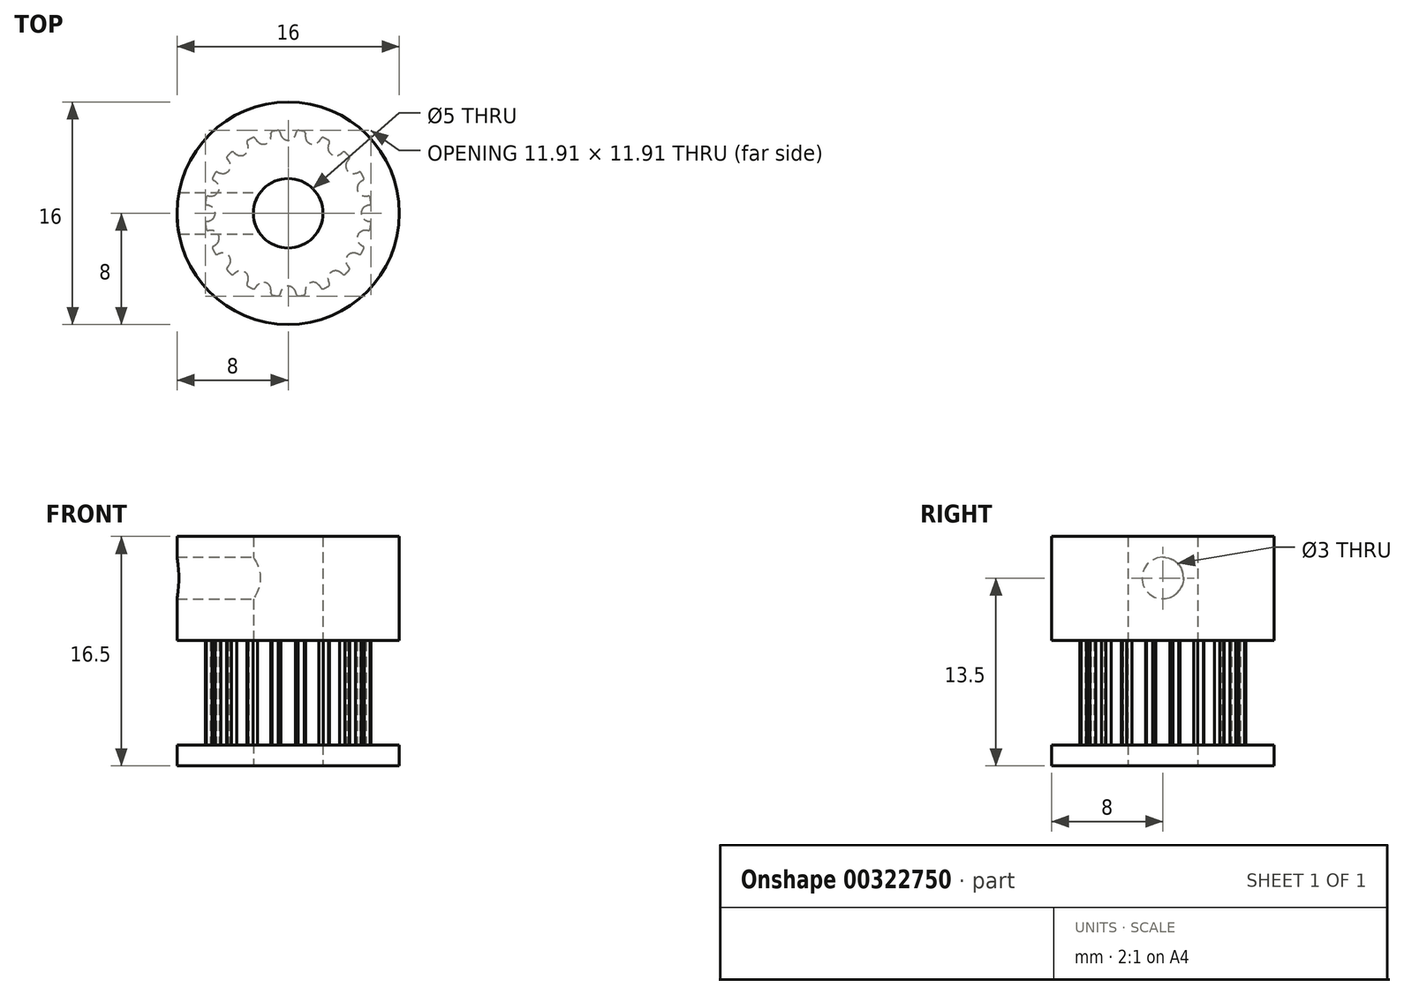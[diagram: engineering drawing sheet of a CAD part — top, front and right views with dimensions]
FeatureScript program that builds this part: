
annotation { "Feature Type Name" : "Feature", "Feature Type Description" : "" }
export const myFeature = defineFeature(function(context is Context, id is Id, definition is map)
    precondition{}
    {
        {
            var Q0;
            Q0=qCreatedBy(makeId("Top.planeOp"),FACE);
            var sketch = newSketch(context, id + "F0", { "sketchPlane" : qUnion([Q0])});
            skLineSegment(sketch, "E0", {"start": v(-19.17, 17.78) * mm, "end": v(-18.17, 17.78) * mm});
            skLineSegment(sketch, "E1", {"start": v(-18.17, 17.78) * mm, "end": v(-18.17, 18.4) * mm});
            skArc(sketch, "E2", {"start": v(-18.67, 18.85) * mm, "mid": v(-18.88, 19.07) * mm, "end": v(-19.17, 19.16) * mm});
            skArc(sketch, "E3", {"start": v(-18.58, 18.54) * mm, "mid": v(-18.61, 18.7) * mm, "end": v(-18.67, 18.85) * mm});
            skArc(sketch, "E4", {"start": v(-18.58, 18.54) * mm, "mid": v(-18.53, 18.44) * mm, "end": v(-18.43, 18.4) * mm});
            skLineSegment(sketch, "E5", {"start": v(-18.43, 18.4) * mm, "end": v(-18.17, 18.4) * mm});
            skArc(sketch, "E6.0.MirrorCS", {"start": v(-19.67, 18.85) * mm, "mid": v(-19.47, 19.07) * mm, "end": v(-19.17, 19.16) * mm});
            skArc(sketch, "E7.0.MirrorCS", {"start": v(-19.76, 18.54) * mm, "mid": v(-19.73, 18.7) * mm, "end": v(-19.67, 18.85) * mm});
            skArc(sketch, "E8.0.MirrorCS", {"start": v(-19.76, 18.54) * mm, "mid": v(-19.81, 18.44) * mm, "end": v(-19.91, 18.4) * mm});
            skLineSegment(sketch, "E9.0.MirrorCS", {"start": v(-19.91, 18.4) * mm, "end": v(-20.17, 18.4) * mm});
            skLineSegment(sketch, "E10.0.MirrorCS", {"start": v(-20.17, 17.78) * mm, "end": v(-20.17, 18.4) * mm});
            skLineSegment(sketch, "E11.0.MirrorCS", {"start": v(-19.17, 17.78) * mm, "end": v(-20.17, 17.78) * mm});
            skLineSegment(sketch, "E12.direction1", {"start": v(-20.17, 17.78) * mm, "end": v(-18.17, 17.78) * mm, "construction": true});
            skLineSegment(sketch, "E13", {"start": v(-20.17, 18.15) * mm, "end": v(-18.17, 18.15) * mm, "construction": true});
            skPoint(sketch, "E14", {"position": v(0, -5.25) * mm});
            skArc(sketch, "E15", {"start": v(0.51, -5.6) * mm, "mid": v(0, -5.25) * mm, "end": v(-0.51, -5.6) * mm});
            skArc(sketch, "E16", {"start": v(-0.51, -5.6) * mm, "mid": v(-0.56, -5.71) * mm, "end": v(-0.59, -5.83) * mm});
            skArc(sketch, "E17", {"start": v(0.59, -5.83) * mm, "mid": v(0.56, -5.71) * mm, "end": v(0.51, -5.6) * mm});
            skArc(sketch, "E18", {"start": v(0.72, -5.96) * mm, "mid": v(0.94, -5.93) * mm, "end": v(1.16, -5.89) * mm});
            skArc(sketch, "E19", {"start": v(0.59, -5.83) * mm, "mid": v(0.66, -5.94) * mm, "end": v(0.8, -5.95) * mm});
            skArc(sketch, "E20", {"start": v(-0.59, -5.83) * mm, "mid": v(-0.66, -5.94) * mm, "end": v(-0.8, -5.95) * mm});
            skArc(sketch, "E21.1.0", {"start": v(2.22, -5.16) * mm, "mid": v(1.62, -5) * mm, "end": v(1.24, -5.48) * mm});
            skPoint(sketch, "E21.1.1", {"position": v(1.62, -5) * mm});
            skArc(sketch, "E21.1.2", {"start": v(1.24, -5.48) * mm, "mid": v(1.23, -5.6) * mm, "end": v(1.24, -5.73) * mm});
            skArc(sketch, "E21.1.3", {"start": v(2.36, -5.37) * mm, "mid": v(2.47, -5.44) * mm, "end": v(2.6, -5.41) * mm});
            skArc(sketch, "E21.1.4", {"start": v(1.24, -5.73) * mm, "mid": v(1.2, -5.85) * mm, "end": v(1.08, -5.9) * mm});
            skArc(sketch, "E21.1.5", {"start": v(2.36, -5.37) * mm, "mid": v(2.3, -5.26) * mm, "end": v(2.22, -5.16) * mm});
            skArc(sketch, "E22.3.2.0", {"start": v(3.7, -4.22) * mm, "mid": v(3.09, -4.25) * mm, "end": v(2.87, -4.83) * mm});
            skPoint(sketch, "E22.4.2.0", {"position": v(3.09, -4.25) * mm});
            skArc(sketch, "E22.5.2.0", {"start": v(2.87, -4.83) * mm, "mid": v(2.9, -4.95) * mm, "end": v(2.95, -5.07) * mm});
            skArc(sketch, "E22.9.2.0", {"start": v(3.9, -4.37) * mm, "mid": v(4.03, -4.41) * mm, "end": v(4.14, -4.35) * mm});
            skArc(sketch, "E22.13.2.0", {"start": v(2.95, -5.07) * mm, "mid": v(2.95, -5.2) * mm, "end": v(2.85, -5.28) * mm});
            skArc(sketch, "E22.17.2.0", {"start": v(3.9, -4.37) * mm, "mid": v(3.81, -4.3) * mm, "end": v(3.7, -4.22) * mm});
            skArc(sketch, "E22.3.3.0", {"start": v(4.83, -2.87) * mm, "mid": v(4.25, -3.09) * mm, "end": v(4.22, -3.7) * mm});
            skPoint(sketch, "E22.4.3.0", {"position": v(4.25, -3.09) * mm});
            skArc(sketch, "E22.5.3.0", {"start": v(4.22, -3.7) * mm, "mid": v(4.3, -3.81) * mm, "end": v(4.37, -3.9) * mm});
            skArc(sketch, "E22.9.3.0", {"start": v(5.07, -2.95) * mm, "mid": v(5.2, -2.95) * mm, "end": v(5.28, -2.85) * mm});
            skArc(sketch, "E22.13.3.0", {"start": v(4.37, -3.9) * mm, "mid": v(4.41, -4.03) * mm, "end": v(4.35, -4.14) * mm});
            skArc(sketch, "E22.17.3.0", {"start": v(5.07, -2.95) * mm, "mid": v(4.95, -2.9) * mm, "end": v(4.83, -2.87) * mm});
            skArc(sketch, "E22.3.4.0", {"start": v(5.48, -1.24) * mm, "mid": v(5, -1.62) * mm, "end": v(5.16, -2.22) * mm});
            skPoint(sketch, "E22.4.4.0", {"position": v(5, -1.62) * mm});
            skArc(sketch, "E22.5.4.0", {"start": v(5.16, -2.22) * mm, "mid": v(5.26, -2.3) * mm, "end": v(5.37, -2.36) * mm});
            skArc(sketch, "E22.9.4.0", {"start": v(5.73, -1.24) * mm, "mid": v(5.85, -1.2) * mm, "end": v(5.9, -1.08) * mm});
            skArc(sketch, "E22.13.4.0", {"start": v(5.37, -2.36) * mm, "mid": v(5.44, -2.47) * mm, "end": v(5.41, -2.6) * mm});
            skArc(sketch, "E22.17.4.0", {"start": v(5.73, -1.24) * mm, "mid": v(5.6, -1.23) * mm, "end": v(5.48, -1.24) * mm});
            skArc(sketch, "E22.3.5.0", {"start": v(5.6, 0.51) * mm, "mid": v(5.25, 0) * mm, "end": v(5.6, -0.51) * mm});
            skPoint(sketch, "E22.4.5.0", {"position": v(5.25, 0) * mm});
            skArc(sketch, "E22.5.5.0", {"start": v(5.6, -0.51) * mm, "mid": v(5.71, -0.56) * mm, "end": v(5.83, -0.59) * mm});
            skArc(sketch, "E22.9.5.0", {"start": v(5.83, 0.59) * mm, "mid": v(5.94, 0.66) * mm, "end": v(5.95, 0.8) * mm});
            skArc(sketch, "E22.13.5.0", {"start": v(5.83, -0.59) * mm, "mid": v(5.94, -0.66) * mm, "end": v(5.95, -0.8) * mm});
            skArc(sketch, "E22.17.5.0", {"start": v(5.83, 0.59) * mm, "mid": v(5.71, 0.56) * mm, "end": v(5.6, 0.51) * mm});
            skArc(sketch, "E22.3.6.0", {"start": v(5.16, 2.22) * mm, "mid": v(5, 1.62) * mm, "end": v(5.48, 1.24) * mm});
            skPoint(sketch, "E22.4.6.0", {"position": v(5, 1.62) * mm});
            skArc(sketch, "E22.5.6.0", {"start": v(5.48, 1.24) * mm, "mid": v(5.6, 1.23) * mm, "end": v(5.73, 1.24) * mm});
            skArc(sketch, "E22.9.6.0", {"start": v(5.37, 2.36) * mm, "mid": v(5.44, 2.47) * mm, "end": v(5.41, 2.6) * mm});
            skArc(sketch, "E22.13.6.0", {"start": v(5.73, 1.24) * mm, "mid": v(5.85, 1.2) * mm, "end": v(5.9, 1.08) * mm});
            skArc(sketch, "E22.17.6.0", {"start": v(5.37, 2.36) * mm, "mid": v(5.26, 2.3) * mm, "end": v(5.16, 2.22) * mm});
            skArc(sketch, "E22.3.7.0", {"start": v(4.22, 3.7) * mm, "mid": v(4.25, 3.09) * mm, "end": v(4.83, 2.87) * mm});
            skPoint(sketch, "E22.4.7.0", {"position": v(4.25, 3.09) * mm});
            skArc(sketch, "E22.5.7.0", {"start": v(4.83, 2.87) * mm, "mid": v(4.95, 2.9) * mm, "end": v(5.07, 2.95) * mm});
            skArc(sketch, "E22.9.7.0", {"start": v(4.37, 3.9) * mm, "mid": v(4.41, 4.03) * mm, "end": v(4.35, 4.14) * mm});
            skArc(sketch, "E22.13.7.0", {"start": v(5.07, 2.95) * mm, "mid": v(5.2, 2.95) * mm, "end": v(5.28, 2.85) * mm});
            skArc(sketch, "E22.17.7.0", {"start": v(4.37, 3.9) * mm, "mid": v(4.3, 3.81) * mm, "end": v(4.22, 3.7) * mm});
            skArc(sketch, "E22.3.8.0", {"start": v(2.87, 4.83) * mm, "mid": v(3.09, 4.25) * mm, "end": v(3.7, 4.22) * mm});
            skPoint(sketch, "E22.4.8.0", {"position": v(3.09, 4.25) * mm});
            skArc(sketch, "E22.5.8.0", {"start": v(3.7, 4.22) * mm, "mid": v(3.81, 4.3) * mm, "end": v(3.9, 4.37) * mm});
            skArc(sketch, "E22.9.8.0", {"start": v(2.95, 5.07) * mm, "mid": v(2.95, 5.2) * mm, "end": v(2.85, 5.28) * mm});
            skArc(sketch, "E22.13.8.0", {"start": v(3.9, 4.37) * mm, "mid": v(4.03, 4.41) * mm, "end": v(4.14, 4.35) * mm});
            skArc(sketch, "E22.17.8.0", {"start": v(2.95, 5.07) * mm, "mid": v(2.9, 4.95) * mm, "end": v(2.87, 4.83) * mm});
            skArc(sketch, "E22.3.9.0", {"start": v(1.24, 5.48) * mm, "mid": v(1.62, 5) * mm, "end": v(2.22, 5.16) * mm});
            skPoint(sketch, "E22.4.9.0", {"position": v(1.62, 5) * mm});
            skArc(sketch, "E22.5.9.0", {"start": v(2.22, 5.16) * mm, "mid": v(2.3, 5.26) * mm, "end": v(2.36, 5.37) * mm});
            skArc(sketch, "E22.9.9.0", {"start": v(1.24, 5.73) * mm, "mid": v(1.2, 5.85) * mm, "end": v(1.08, 5.9) * mm});
            skArc(sketch, "E22.13.9.0", {"start": v(2.36, 5.37) * mm, "mid": v(2.47, 5.44) * mm, "end": v(2.6, 5.41) * mm});
            skArc(sketch, "E22.17.9.0", {"start": v(1.24, 5.73) * mm, "mid": v(1.23, 5.6) * mm, "end": v(1.24, 5.48) * mm});
            skArc(sketch, "E22.3.10.0", {"start": v(-0.51, 5.6) * mm, "mid": v(0, 5.25) * mm, "end": v(0.51, 5.6) * mm});
            skPoint(sketch, "E22.4.10.0", {"position": v(0, 5.25) * mm});
            skArc(sketch, "E22.5.10.0", {"start": v(0.51, 5.6) * mm, "mid": v(0.56, 5.71) * mm, "end": v(0.59, 5.83) * mm});
            skArc(sketch, "E22.9.10.0", {"start": v(-0.59, 5.83) * mm, "mid": v(-0.66, 5.94) * mm, "end": v(-0.8, 5.95) * mm});
            skArc(sketch, "E22.13.10.0", {"start": v(0.59, 5.83) * mm, "mid": v(0.66, 5.94) * mm, "end": v(0.8, 5.95) * mm});
            skArc(sketch, "E22.17.10.0", {"start": v(-0.59, 5.83) * mm, "mid": v(-0.56, 5.71) * mm, "end": v(-0.51, 5.6) * mm});
            skArc(sketch, "E22.3.11.0", {"start": v(-2.22, 5.16) * mm, "mid": v(-1.62, 5) * mm, "end": v(-1.24, 5.48) * mm});
            skPoint(sketch, "E22.4.11.0", {"position": v(-1.62, 5) * mm});
            skArc(sketch, "E22.5.11.0", {"start": v(-1.24, 5.48) * mm, "mid": v(-1.23, 5.6) * mm, "end": v(-1.24, 5.73) * mm});
            skArc(sketch, "E22.9.11.0", {"start": v(-2.36, 5.37) * mm, "mid": v(-2.47, 5.44) * mm, "end": v(-2.6, 5.41) * mm});
            skArc(sketch, "E22.13.11.0", {"start": v(-1.24, 5.73) * mm, "mid": v(-1.2, 5.85) * mm, "end": v(-1.08, 5.9) * mm});
            skArc(sketch, "E22.17.11.0", {"start": v(-2.36, 5.37) * mm, "mid": v(-2.3, 5.26) * mm, "end": v(-2.22, 5.16) * mm});
            skArc(sketch, "E22.3.12.0", {"start": v(-3.7, 4.22) * mm, "mid": v(-3.09, 4.25) * mm, "end": v(-2.87, 4.83) * mm});
            skPoint(sketch, "E22.4.12.0", {"position": v(-3.09, 4.25) * mm});
            skArc(sketch, "E22.5.12.0", {"start": v(-2.87, 4.83) * mm, "mid": v(-2.9, 4.95) * mm, "end": v(-2.95, 5.07) * mm});
            skArc(sketch, "E22.9.12.0", {"start": v(-3.9, 4.37) * mm, "mid": v(-4.03, 4.41) * mm, "end": v(-4.14, 4.35) * mm});
            skArc(sketch, "E22.13.12.0", {"start": v(-2.95, 5.07) * mm, "mid": v(-2.95, 5.2) * mm, "end": v(-2.85, 5.28) * mm});
            skArc(sketch, "E22.17.12.0", {"start": v(-3.9, 4.37) * mm, "mid": v(-3.81, 4.3) * mm, "end": v(-3.7, 4.22) * mm});
            skArc(sketch, "E22.3.13.0", {"start": v(-4.83, 2.87) * mm, "mid": v(-4.25, 3.09) * mm, "end": v(-4.22, 3.7) * mm});
            skPoint(sketch, "E22.4.13.0", {"position": v(-4.25, 3.09) * mm});
            skArc(sketch, "E22.5.13.0", {"start": v(-4.22, 3.7) * mm, "mid": v(-4.3, 3.81) * mm, "end": v(-4.37, 3.9) * mm});
            skArc(sketch, "E22.9.13.0", {"start": v(-5.07, 2.95) * mm, "mid": v(-5.2, 2.95) * mm, "end": v(-5.28, 2.85) * mm});
            skArc(sketch, "E22.13.13.0", {"start": v(-4.37, 3.9) * mm, "mid": v(-4.41, 4.03) * mm, "end": v(-4.35, 4.14) * mm});
            skArc(sketch, "E22.17.13.0", {"start": v(-5.07, 2.95) * mm, "mid": v(-4.95, 2.9) * mm, "end": v(-4.83, 2.87) * mm});
            skArc(sketch, "E22.3.14.0", {"start": v(-5.48, 1.24) * mm, "mid": v(-5, 1.62) * mm, "end": v(-5.16, 2.22) * mm});
            skPoint(sketch, "E22.4.14.0", {"position": v(-5, 1.62) * mm});
            skArc(sketch, "E22.5.14.0", {"start": v(-5.16, 2.22) * mm, "mid": v(-5.26, 2.3) * mm, "end": v(-5.37, 2.36) * mm});
            skArc(sketch, "E22.9.14.0", {"start": v(-5.73, 1.24) * mm, "mid": v(-5.85, 1.2) * mm, "end": v(-5.9, 1.08) * mm});
            skArc(sketch, "E22.13.14.0", {"start": v(-5.37, 2.36) * mm, "mid": v(-5.44, 2.47) * mm, "end": v(-5.41, 2.6) * mm});
            skArc(sketch, "E22.17.14.0", {"start": v(-5.73, 1.24) * mm, "mid": v(-5.6, 1.23) * mm, "end": v(-5.48, 1.24) * mm});
            skArc(sketch, "E22.3.15.0", {"start": v(-5.6, -0.51) * mm, "mid": v(-5.25, 0) * mm, "end": v(-5.6, 0.51) * mm});
            skPoint(sketch, "E22.4.15.0", {"position": v(-5.25, 0) * mm});
            skArc(sketch, "E22.5.15.0", {"start": v(-5.6, 0.51) * mm, "mid": v(-5.71, 0.56) * mm, "end": v(-5.83, 0.59) * mm});
            skArc(sketch, "E22.9.15.0", {"start": v(-5.83, -0.59) * mm, "mid": v(-5.94, -0.66) * mm, "end": v(-5.95, -0.8) * mm});
            skArc(sketch, "E22.13.15.0", {"start": v(-5.83, 0.59) * mm, "mid": v(-5.94, 0.66) * mm, "end": v(-5.95, 0.8) * mm});
            skArc(sketch, "E22.17.15.0", {"start": v(-5.83, -0.59) * mm, "mid": v(-5.71, -0.56) * mm, "end": v(-5.6, -0.51) * mm});
            skArc(sketch, "E22.3.16.0", {"start": v(-5.16, -2.22) * mm, "mid": v(-5, -1.62) * mm, "end": v(-5.48, -1.24) * mm});
            skPoint(sketch, "E22.4.16.0", {"position": v(-5, -1.62) * mm});
            skArc(sketch, "E22.5.16.0", {"start": v(-5.48, -1.24) * mm, "mid": v(-5.6, -1.23) * mm, "end": v(-5.73, -1.24) * mm});
            skArc(sketch, "E22.9.16.0", {"start": v(-5.37, -2.36) * mm, "mid": v(-5.44, -2.47) * mm, "end": v(-5.41, -2.6) * mm});
            skArc(sketch, "E22.13.16.0", {"start": v(-5.73, -1.24) * mm, "mid": v(-5.85, -1.2) * mm, "end": v(-5.9, -1.08) * mm});
            skArc(sketch, "E22.17.16.0", {"start": v(-5.37, -2.36) * mm, "mid": v(-5.26, -2.3) * mm, "end": v(-5.16, -2.22) * mm});
            skArc(sketch, "E22.3.17.0", {"start": v(-4.22, -3.7) * mm, "mid": v(-4.25, -3.09) * mm, "end": v(-4.83, -2.87) * mm});
            skPoint(sketch, "E22.4.17.0", {"position": v(-4.25, -3.09) * mm});
            skArc(sketch, "E22.5.17.0", {"start": v(-4.83, -2.87) * mm, "mid": v(-4.95, -2.9) * mm, "end": v(-5.07, -2.95) * mm});
            skArc(sketch, "E22.9.17.0", {"start": v(-4.37, -3.9) * mm, "mid": v(-4.41, -4.03) * mm, "end": v(-4.35, -4.14) * mm});
            skArc(sketch, "E22.13.17.0", {"start": v(-5.07, -2.95) * mm, "mid": v(-5.2, -2.95) * mm, "end": v(-5.28, -2.85) * mm});
            skArc(sketch, "E22.17.17.0", {"start": v(-4.37, -3.9) * mm, "mid": v(-4.3, -3.81) * mm, "end": v(-4.22, -3.7) * mm});
            skArc(sketch, "E22.3.18.0", {"start": v(-2.87, -4.83) * mm, "mid": v(-3.09, -4.25) * mm, "end": v(-3.7, -4.22) * mm});
            skPoint(sketch, "E22.4.18.0", {"position": v(-3.09, -4.25) * mm});
            skArc(sketch, "E22.5.18.0", {"start": v(-3.7, -4.22) * mm, "mid": v(-3.81, -4.3) * mm, "end": v(-3.9, -4.37) * mm});
            skArc(sketch, "E22.9.18.0", {"start": v(-2.95, -5.07) * mm, "mid": v(-2.95, -5.2) * mm, "end": v(-2.85, -5.28) * mm});
            skArc(sketch, "E22.13.18.0", {"start": v(-3.9, -4.37) * mm, "mid": v(-4.03, -4.41) * mm, "end": v(-4.14, -4.35) * mm});
            skArc(sketch, "E22.17.18.0", {"start": v(-2.95, -5.07) * mm, "mid": v(-2.9, -4.95) * mm, "end": v(-2.87, -4.83) * mm});
            skArc(sketch, "E22.3.19.0", {"start": v(-1.24, -5.48) * mm, "mid": v(-1.62, -5) * mm, "end": v(-2.22, -5.16) * mm});
            skPoint(sketch, "E22.4.19.0", {"position": v(-1.62, -5) * mm});
            skArc(sketch, "E22.5.19.0", {"start": v(-2.22, -5.16) * mm, "mid": v(-2.3, -5.26) * mm, "end": v(-2.36, -5.37) * mm});
            skArc(sketch, "E22.9.19.0", {"start": v(-1.24, -5.73) * mm, "mid": v(-1.2, -5.85) * mm, "end": v(-1.08, -5.9) * mm});
            skArc(sketch, "E22.13.19.0", {"start": v(-2.36, -5.37) * mm, "mid": v(-2.47, -5.44) * mm, "end": v(-2.6, -5.41) * mm});
            skArc(sketch, "E22.17.19.0", {"start": v(-1.24, -5.73) * mm, "mid": v(-1.23, -5.6) * mm, "end": v(-1.24, -5.48) * mm});
            skArc(sketch, "E23.trimOffspring", {"start": v(2.52, -5.44) * mm, "mid": v(2.72, -5.35) * mm, "end": v(2.92, -5.24) * mm});
            skArc(sketch, "E24.trimOffspring", {"start": v(4.08, -4.4) * mm, "mid": v(4.24, -4.24) * mm, "end": v(4.4, -4.08) * mm});
            skArc(sketch, "E25.trimOffspring", {"start": v(5.24, -2.92) * mm, "mid": v(5.33, -2.76) * mm, "end": v(5.41, -2.6) * mm});
            skArc(sketch, "E26.trimOffspring", {"start": v(5.89, -1.16) * mm, "mid": v(5.93, -0.94) * mm, "end": v(5.96, -0.72) * mm});
            skArc(sketch, "E27.trimOffspring", {"start": v(5.44, 2.52) * mm, "mid": v(5.35, 2.72) * mm, "end": v(5.24, 2.92) * mm});
            skArc(sketch, "E28.trimOffspring", {"start": v(4.4, 4.08) * mm, "mid": v(4.24, 4.24) * mm, "end": v(4.08, 4.4) * mm});
            skArc(sketch, "E29.trimOffspring", {"start": v(5.96, 0.72) * mm, "mid": v(5.93, 0.94) * mm, "end": v(5.89, 1.16) * mm});
            skArc(sketch, "E30.trimOffspring", {"start": v(2.92, 5.24) * mm, "mid": v(2.72, 5.35) * mm, "end": v(2.52, 5.44) * mm});
            skArc(sketch, "E31.trimOffspring", {"start": v(1.16, 5.89) * mm, "mid": v(0.94, 5.93) * mm, "end": v(0.72, 5.96) * mm});
            skArc(sketch, "E32.trimOffspring", {"start": v(-0.72, 5.96) * mm, "mid": v(-0.94, 5.93) * mm, "end": v(-1.16, 5.89) * mm});
            skArc(sketch, "E33.trimOffspring", {"start": v(-2.52, 5.44) * mm, "mid": v(-2.72, 5.35) * mm, "end": v(-2.92, 5.24) * mm});
            skArc(sketch, "E34.trimOffspring", {"start": v(-4.08, 4.4) * mm, "mid": v(-4.24, 4.24) * mm, "end": v(-4.4, 4.08) * mm});
            skArc(sketch, "E35.trimOffspring", {"start": v(-5.24, 2.92) * mm, "mid": v(-5.35, 2.72) * mm, "end": v(-5.44, 2.52) * mm});
            skArc(sketch, "E36.trimOffspring", {"start": v(-5.89, 1.16) * mm, "mid": v(-5.93, 0.94) * mm, "end": v(-5.96, 0.72) * mm});
            skArc(sketch, "E37.trimOffspring", {"start": v(-5.96, -0.72) * mm, "mid": v(-5.93, -0.94) * mm, "end": v(-5.89, -1.16) * mm});
            skArc(sketch, "E38.trimOffspring", {"start": v(-5.44, -2.52) * mm, "mid": v(-5.35, -2.72) * mm, "end": v(-5.24, -2.92) * mm});
            skArc(sketch, "E39.trimOffspring", {"start": v(-4.4, -4.08) * mm, "mid": v(-4.24, -4.24) * mm, "end": v(-4.08, -4.4) * mm});
            skArc(sketch, "E40.trimOffspring", {"start": v(-2.92, -5.24) * mm, "mid": v(-2.72, -5.35) * mm, "end": v(-2.52, -5.44) * mm});
            skArc(sketch, "E41.trimOffspring", {"start": v(-1.16, -5.89) * mm, "mid": v(-0.94, -5.93) * mm, "end": v(-0.72, -5.96) * mm});
            skSolve(sketch);
        }
        {
            var Q0;
            Q0=makeQuery(id+"F0.imprint","IMPRINT",FACE,{"disambiguationData":[TD([[makeQuery(id+"F0.imprint","IMPRINT",EDGE,{"derivedFrom":sQuery(id+"F0.wireOp",EDGE,"E15")}),-1.0]])]});
            extrude(context, id + "F1", {"entities" : qUnion([Q0]), "depth" : 7.5 * mm});
        }
        {
            var Q0;
            Q0=makeQuery(id+"F1.opExtrude","CAP_FACE",FACE,{"disambiguationData":[OSD([sQuery(id+"F0.wireOp",EDGE,"E15"),sQuery(id+"F0.wireOp",EDGE,"E16"),sQuery(id+"F0.wireOp",EDGE,"E17"),sQuery(id+"F0.wireOp",EDGE,"E18"),sQuery(id+"F0.wireOp",EDGE,"E19"),sQuery(id+"F0.wireOp",EDGE,"E20"),sQuery(id+"F0.wireOp",EDGE,"E21.1.0"),sQuery(id+"F0.wireOp",EDGE,"E21.1.2"),sQuery(id+"F0.wireOp",EDGE,"E21.1.3"),sQuery(id+"F0.wireOp",EDGE,"E21.1.4"),sQuery(id+"F0.wireOp",EDGE,"E21.1.5"),sQuery(id+"F0.wireOp",EDGE,"E22.3.2.0"),sQuery(id+"F0.wireOp",EDGE,"E22.5.2.0"),sQuery(id+"F0.wireOp",EDGE,"E22.9.2.0"),sQuery(id+"F0.wireOp",EDGE,"E22.13.2.0"),sQuery(id+"F0.wireOp",EDGE,"E22.17.2.0"),sQuery(id+"F0.wireOp",EDGE,"E22.3.3.0"),sQuery(id+"F0.wireOp",EDGE,"E22.5.3.0"),sQuery(id+"F0.wireOp",EDGE,"E22.9.3.0"),sQuery(id+"F0.wireOp",EDGE,"E22.13.3.0"),sQuery(id+"F0.wireOp",EDGE,"E22.17.3.0"),sQuery(id+"F0.wireOp",EDGE,"E22.3.4.0"),sQuery(id+"F0.wireOp",EDGE,"E22.5.4.0"),sQuery(id+"F0.wireOp",EDGE,"E22.9.4.0"),sQuery(id+"F0.wireOp",EDGE,"E22.13.4.0"),sQuery(id+"F0.wireOp",EDGE,"E22.17.4.0"),sQuery(id+"F0.wireOp",EDGE,"E22.3.5.0"),sQuery(id+"F0.wireOp",EDGE,"E22.5.5.0"),sQuery(id+"F0.wireOp",EDGE,"E22.9.5.0"),sQuery(id+"F0.wireOp",EDGE,"E22.13.5.0"),sQuery(id+"F0.wireOp",EDGE,"E22.17.5.0"),sQuery(id+"F0.wireOp",EDGE,"E22.3.6.0"),sQuery(id+"F0.wireOp",EDGE,"E22.5.6.0"),sQuery(id+"F0.wireOp",EDGE,"E22.9.6.0"),sQuery(id+"F0.wireOp",EDGE,"E22.13.6.0"),sQuery(id+"F0.wireOp",EDGE,"E22.17.6.0"),sQuery(id+"F0.wireOp",EDGE,"E22.3.7.0"),sQuery(id+"F0.wireOp",EDGE,"E22.5.7.0"),sQuery(id+"F0.wireOp",EDGE,"E22.9.7.0"),sQuery(id+"F0.wireOp",EDGE,"E22.13.7.0"),sQuery(id+"F0.wireOp",EDGE,"E22.17.7.0"),sQuery(id+"F0.wireOp",EDGE,"E22.3.8.0"),sQuery(id+"F0.wireOp",EDGE,"E22.5.8.0"),sQuery(id+"F0.wireOp",EDGE,"E22.9.8.0"),sQuery(id+"F0.wireOp",EDGE,"E22.13.8.0"),sQuery(id+"F0.wireOp",EDGE,"E22.17.8.0"),sQuery(id+"F0.wireOp",EDGE,"E22.3.9.0"),sQuery(id+"F0.wireOp",EDGE,"E22.5.9.0"),sQuery(id+"F0.wireOp",EDGE,"E22.9.9.0"),sQuery(id+"F0.wireOp",EDGE,"E22.13.9.0"),sQuery(id+"F0.wireOp",EDGE,"E22.17.9.0"),sQuery(id+"F0.wireOp",EDGE,"E22.3.10.0"),sQuery(id+"F0.wireOp",EDGE,"E22.5.10.0"),sQuery(id+"F0.wireOp",EDGE,"E22.9.10.0"),sQuery(id+"F0.wireOp",EDGE,"E22.13.10.0"),sQuery(id+"F0.wireOp",EDGE,"E22.17.10.0"),sQuery(id+"F0.wireOp",EDGE,"E22.3.11.0"),sQuery(id+"F0.wireOp",EDGE,"E22.5.11.0"),sQuery(id+"F0.wireOp",EDGE,"E22.9.11.0"),sQuery(id+"F0.wireOp",EDGE,"E22.13.11.0"),sQuery(id+"F0.wireOp",EDGE,"E22.17.11.0"),sQuery(id+"F0.wireOp",EDGE,"E22.3.12.0"),sQuery(id+"F0.wireOp",EDGE,"E22.5.12.0"),sQuery(id+"F0.wireOp",EDGE,"E22.9.12.0"),sQuery(id+"F0.wireOp",EDGE,"E22.13.12.0"),sQuery(id+"F0.wireOp",EDGE,"E22.17.12.0"),sQuery(id+"F0.wireOp",EDGE,"E22.3.13.0"),sQuery(id+"F0.wireOp",EDGE,"E22.5.13.0"),sQuery(id+"F0.wireOp",EDGE,"E22.9.13.0"),sQuery(id+"F0.wireOp",EDGE,"E22.13.13.0"),sQuery(id+"F0.wireOp",EDGE,"E22.17.13.0"),sQuery(id+"F0.wireOp",EDGE,"E22.3.14.0"),sQuery(id+"F0.wireOp",EDGE,"E22.5.14.0"),sQuery(id+"F0.wireOp",EDGE,"E22.9.14.0"),sQuery(id+"F0.wireOp",EDGE,"E22.13.14.0"),sQuery(id+"F0.wireOp",EDGE,"E22.17.14.0"),sQuery(id+"F0.wireOp",EDGE,"E22.3.15.0"),sQuery(id+"F0.wireOp",EDGE,"E22.5.15.0"),sQuery(id+"F0.wireOp",EDGE,"E22.9.15.0"),sQuery(id+"F0.wireOp",EDGE,"E22.13.15.0"),sQuery(id+"F0.wireOp",EDGE,"E22.17.15.0"),sQuery(id+"F0.wireOp",EDGE,"E22.3.16.0"),sQuery(id+"F0.wireOp",EDGE,"E22.5.16.0"),sQuery(id+"F0.wireOp",EDGE,"E22.9.16.0"),sQuery(id+"F0.wireOp",EDGE,"E22.13.16.0"),sQuery(id+"F0.wireOp",EDGE,"E22.17.16.0"),sQuery(id+"F0.wireOp",EDGE,"E22.3.17.0"),sQuery(id+"F0.wireOp",EDGE,"E22.5.17.0"),sQuery(id+"F0.wireOp",EDGE,"E22.9.17.0"),sQuery(id+"F0.wireOp",EDGE,"E22.13.17.0"),sQuery(id+"F0.wireOp",EDGE,"E22.17.17.0"),sQuery(id+"F0.wireOp",EDGE,"E22.3.18.0"),sQuery(id+"F0.wireOp",EDGE,"E22.5.18.0"),sQuery(id+"F0.wireOp",EDGE,"E22.9.18.0"),sQuery(id+"F0.wireOp",EDGE,"E22.13.18.0"),sQuery(id+"F0.wireOp",EDGE,"E22.17.18.0"),sQuery(id+"F0.wireOp",EDGE,"E22.3.19.0"),sQuery(id+"F0.wireOp",EDGE,"E22.5.19.0"),sQuery(id+"F0.wireOp",EDGE,"E22.9.19.0"),sQuery(id+"F0.wireOp",EDGE,"E22.13.19.0"),sQuery(id+"F0.wireOp",EDGE,"E22.17.19.0"),sQuery(id+"F0.wireOp",EDGE,"E23.trimOffspring"),sQuery(id+"F0.wireOp",EDGE,"E24.trimOffspring"),sQuery(id+"F0.wireOp",EDGE,"E25.trimOffspring"),sQuery(id+"F0.wireOp",EDGE,"E26.trimOffspring"),sQuery(id+"F0.wireOp",EDGE,"E27.trimOffspring"),sQuery(id+"F0.wireOp",EDGE,"E28.trimOffspring"),sQuery(id+"F0.wireOp",EDGE,"E29.trimOffspring"),sQuery(id+"F0.wireOp",EDGE,"E30.trimOffspring"),sQuery(id+"F0.wireOp",EDGE,"E31.trimOffspring"),sQuery(id+"F0.wireOp",EDGE,"E32.trimOffspring"),sQuery(id+"F0.wireOp",EDGE,"E33.trimOffspring"),sQuery(id+"F0.wireOp",EDGE,"E34.trimOffspring"),sQuery(id+"F0.wireOp",EDGE,"E35.trimOffspring"),sQuery(id+"F0.wireOp",EDGE,"E36.trimOffspring"),sQuery(id+"F0.wireOp",EDGE,"E37.trimOffspring"),sQuery(id+"F0.wireOp",EDGE,"E38.trimOffspring"),sQuery(id+"F0.wireOp",EDGE,"E39.trimOffspring"),sQuery(id+"F0.wireOp",EDGE,"E40.trimOffspring"),sQuery(id+"F0.wireOp",EDGE,"E41.trimOffspring")])],"isStart":false});
            var sketch = newSketch(context, id + "F2", { "sketchPlane" : qUnion([Q0])});
            skCircle(sketch, "E42", {"center": v(0, 0) * mm, "radius": 8 * mm});
            skSolve(sketch);
        }
        {
            var Q0;
            Q0=qSketchRegion(id+"F2",true);
            extrude(context, id + "F3", {"entities" : qUnion([Q0]), "operationType" : NewBodyOperationType.ADD, "depth" : 9 * mm});
        }
        {
            var Q0;
            Q0=makeQuery(id+"F1.opExtrude","CAP_FACE",FACE,{"disambiguationData":[OSD([sQuery(id+"F0.wireOp",EDGE,"E15"),sQuery(id+"F0.wireOp",EDGE,"E16"),sQuery(id+"F0.wireOp",EDGE,"E17"),sQuery(id+"F0.wireOp",EDGE,"E18"),sQuery(id+"F0.wireOp",EDGE,"E19"),sQuery(id+"F0.wireOp",EDGE,"E20"),sQuery(id+"F0.wireOp",EDGE,"E21.1.0"),sQuery(id+"F0.wireOp",EDGE,"E21.1.2"),sQuery(id+"F0.wireOp",EDGE,"E21.1.3"),sQuery(id+"F0.wireOp",EDGE,"E21.1.4"),sQuery(id+"F0.wireOp",EDGE,"E21.1.5"),sQuery(id+"F0.wireOp",EDGE,"E22.3.2.0"),sQuery(id+"F0.wireOp",EDGE,"E22.5.2.0"),sQuery(id+"F0.wireOp",EDGE,"E22.9.2.0"),sQuery(id+"F0.wireOp",EDGE,"E22.13.2.0"),sQuery(id+"F0.wireOp",EDGE,"E22.17.2.0"),sQuery(id+"F0.wireOp",EDGE,"E22.3.3.0"),sQuery(id+"F0.wireOp",EDGE,"E22.5.3.0"),sQuery(id+"F0.wireOp",EDGE,"E22.9.3.0"),sQuery(id+"F0.wireOp",EDGE,"E22.13.3.0"),sQuery(id+"F0.wireOp",EDGE,"E22.17.3.0"),sQuery(id+"F0.wireOp",EDGE,"E22.3.4.0"),sQuery(id+"F0.wireOp",EDGE,"E22.5.4.0"),sQuery(id+"F0.wireOp",EDGE,"E22.9.4.0"),sQuery(id+"F0.wireOp",EDGE,"E22.13.4.0"),sQuery(id+"F0.wireOp",EDGE,"E22.17.4.0"),sQuery(id+"F0.wireOp",EDGE,"E22.3.5.0"),sQuery(id+"F0.wireOp",EDGE,"E22.5.5.0"),sQuery(id+"F0.wireOp",EDGE,"E22.9.5.0"),sQuery(id+"F0.wireOp",EDGE,"E22.13.5.0"),sQuery(id+"F0.wireOp",EDGE,"E22.17.5.0"),sQuery(id+"F0.wireOp",EDGE,"E22.3.6.0"),sQuery(id+"F0.wireOp",EDGE,"E22.5.6.0"),sQuery(id+"F0.wireOp",EDGE,"E22.9.6.0"),sQuery(id+"F0.wireOp",EDGE,"E22.13.6.0"),sQuery(id+"F0.wireOp",EDGE,"E22.17.6.0"),sQuery(id+"F0.wireOp",EDGE,"E22.3.7.0"),sQuery(id+"F0.wireOp",EDGE,"E22.5.7.0"),sQuery(id+"F0.wireOp",EDGE,"E22.9.7.0"),sQuery(id+"F0.wireOp",EDGE,"E22.13.7.0"),sQuery(id+"F0.wireOp",EDGE,"E22.17.7.0"),sQuery(id+"F0.wireOp",EDGE,"E22.3.8.0"),sQuery(id+"F0.wireOp",EDGE,"E22.5.8.0"),sQuery(id+"F0.wireOp",EDGE,"E22.9.8.0"),sQuery(id+"F0.wireOp",EDGE,"E22.13.8.0"),sQuery(id+"F0.wireOp",EDGE,"E22.17.8.0"),sQuery(id+"F0.wireOp",EDGE,"E22.3.9.0"),sQuery(id+"F0.wireOp",EDGE,"E22.5.9.0"),sQuery(id+"F0.wireOp",EDGE,"E22.9.9.0"),sQuery(id+"F0.wireOp",EDGE,"E22.13.9.0"),sQuery(id+"F0.wireOp",EDGE,"E22.17.9.0"),sQuery(id+"F0.wireOp",EDGE,"E22.3.10.0"),sQuery(id+"F0.wireOp",EDGE,"E22.5.10.0"),sQuery(id+"F0.wireOp",EDGE,"E22.9.10.0"),sQuery(id+"F0.wireOp",EDGE,"E22.13.10.0"),sQuery(id+"F0.wireOp",EDGE,"E22.17.10.0"),sQuery(id+"F0.wireOp",EDGE,"E22.3.11.0"),sQuery(id+"F0.wireOp",EDGE,"E22.5.11.0"),sQuery(id+"F0.wireOp",EDGE,"E22.9.11.0"),sQuery(id+"F0.wireOp",EDGE,"E22.13.11.0"),sQuery(id+"F0.wireOp",EDGE,"E22.17.11.0"),sQuery(id+"F0.wireOp",EDGE,"E22.3.12.0"),sQuery(id+"F0.wireOp",EDGE,"E22.5.12.0"),sQuery(id+"F0.wireOp",EDGE,"E22.9.12.0"),sQuery(id+"F0.wireOp",EDGE,"E22.13.12.0"),sQuery(id+"F0.wireOp",EDGE,"E22.17.12.0"),sQuery(id+"F0.wireOp",EDGE,"E22.3.13.0"),sQuery(id+"F0.wireOp",EDGE,"E22.5.13.0"),sQuery(id+"F0.wireOp",EDGE,"E22.9.13.0"),sQuery(id+"F0.wireOp",EDGE,"E22.13.13.0"),sQuery(id+"F0.wireOp",EDGE,"E22.17.13.0"),sQuery(id+"F0.wireOp",EDGE,"E22.3.14.0"),sQuery(id+"F0.wireOp",EDGE,"E22.5.14.0"),sQuery(id+"F0.wireOp",EDGE,"E22.9.14.0"),sQuery(id+"F0.wireOp",EDGE,"E22.13.14.0"),sQuery(id+"F0.wireOp",EDGE,"E22.17.14.0"),sQuery(id+"F0.wireOp",EDGE,"E22.3.15.0"),sQuery(id+"F0.wireOp",EDGE,"E22.5.15.0"),sQuery(id+"F0.wireOp",EDGE,"E22.9.15.0"),sQuery(id+"F0.wireOp",EDGE,"E22.13.15.0"),sQuery(id+"F0.wireOp",EDGE,"E22.17.15.0"),sQuery(id+"F0.wireOp",EDGE,"E22.3.16.0"),sQuery(id+"F0.wireOp",EDGE,"E22.5.16.0"),sQuery(id+"F0.wireOp",EDGE,"E22.9.16.0"),sQuery(id+"F0.wireOp",EDGE,"E22.13.16.0"),sQuery(id+"F0.wireOp",EDGE,"E22.17.16.0"),sQuery(id+"F0.wireOp",EDGE,"E22.3.17.0"),sQuery(id+"F0.wireOp",EDGE,"E22.5.17.0"),sQuery(id+"F0.wireOp",EDGE,"E22.9.17.0"),sQuery(id+"F0.wireOp",EDGE,"E22.13.17.0"),sQuery(id+"F0.wireOp",EDGE,"E22.17.17.0"),sQuery(id+"F0.wireOp",EDGE,"E22.3.18.0"),sQuery(id+"F0.wireOp",EDGE,"E22.5.18.0"),sQuery(id+"F0.wireOp",EDGE,"E22.9.18.0"),sQuery(id+"F0.wireOp",EDGE,"E22.13.18.0"),sQuery(id+"F0.wireOp",EDGE,"E22.17.18.0"),sQuery(id+"F0.wireOp",EDGE,"E22.3.19.0"),sQuery(id+"F0.wireOp",EDGE,"E22.5.19.0"),sQuery(id+"F0.wireOp",EDGE,"E22.9.19.0"),sQuery(id+"F0.wireOp",EDGE,"E22.13.19.0"),sQuery(id+"F0.wireOp",EDGE,"E22.17.19.0"),sQuery(id+"F0.wireOp",EDGE,"E23.trimOffspring"),sQuery(id+"F0.wireOp",EDGE,"E24.trimOffspring"),sQuery(id+"F0.wireOp",EDGE,"E25.trimOffspring"),sQuery(id+"F0.wireOp",EDGE,"E26.trimOffspring"),sQuery(id+"F0.wireOp",EDGE,"E27.trimOffspring"),sQuery(id+"F0.wireOp",EDGE,"E28.trimOffspring"),sQuery(id+"F0.wireOp",EDGE,"E29.trimOffspring"),sQuery(id+"F0.wireOp",EDGE,"E30.trimOffspring"),sQuery(id+"F0.wireOp",EDGE,"E31.trimOffspring"),sQuery(id+"F0.wireOp",EDGE,"E32.trimOffspring"),sQuery(id+"F0.wireOp",EDGE,"E33.trimOffspring"),sQuery(id+"F0.wireOp",EDGE,"E34.trimOffspring"),sQuery(id+"F0.wireOp",EDGE,"E35.trimOffspring"),sQuery(id+"F0.wireOp",EDGE,"E36.trimOffspring"),sQuery(id+"F0.wireOp",EDGE,"E37.trimOffspring"),sQuery(id+"F0.wireOp",EDGE,"E38.trimOffspring"),sQuery(id+"F0.wireOp",EDGE,"E39.trimOffspring"),sQuery(id+"F0.wireOp",EDGE,"E40.trimOffspring"),sQuery(id+"F0.wireOp",EDGE,"E41.trimOffspring")])],"isStart":true});
            var sketch = newSketch(context, id + "F4", { "sketchPlane" : qUnion([Q0])});
            skCircle(sketch, "E43", {"center": v(0, 0) * mm, "radius": 8 * mm});
            skSolve(sketch);
        }
        {
            var Q0;
            Q0=qSketchRegion(id+"F4",true);
            extrude(context, id + "F5", {"entities" : qUnion([Q0]), "operationType" : NewBodyOperationType.ADD, "depth" : 1.5 * mm});
        }
        {
            var Q0;
            Q0=makeQuery(id+"F5.opExtrude","CAP_FACE",FACE,{"disambiguationData":[OSD([sQuery(id+"F4.wireOp",EDGE,"E43")])],"isStart":false});
            var sketch = newSketch(context, id + "F6", { "sketchPlane" : qUnion([Q0])});
            skCircle(sketch, "E44", {"center": v(0, 0) * mm, "radius": 2.5 * mm});
            skSolve(sketch);
        }
        {
            var Q0;
            Q0=qSketchRegion(id+"F6",true);
            extrude(context, id + "F7", {"entities" : qUnion([Q0]), "operationType" : NewBodyOperationType.REMOVE, "endBound" : BoundingType.THROUGH_ALL, "oppositeDirection" : true, "depth" : 25 * mm});
        }
        {
            var Q0;
            Q0=qCreatedBy(makeId("Right.planeOp"),FACE);
            var sketch = newSketch(context, id + "F8", { "sketchPlane" : qUnion([Q0])});
            skCircle(sketch, "E45", {"center": v(0, 12) * mm, "radius": 1.5 * mm});
            skSolve(sketch);
        }
        {
            var Q0;
            Q0=qSketchRegion(id+"F8",true);
            extrude(context, id + "F9", {"entities" : qUnion([Q0]), "operationType" : NewBodyOperationType.REMOVE, "endBound" : BoundingType.THROUGH_ALL, "oppositeDirection" : true, "depth" : 25 * mm});
        }
        {
            var Q0;
            Q0=makeQuery(id+"F3.opExtrude","CAP_FACE",FACE,{"disambiguationData":[OSD([sQuery(id+"F2.wireOp",EDGE,"E42")])],"isStart":false});
            extrude(context, id + "F10", {"entities" : qUnion([Q0]), "operationType" : NewBodyOperationType.REMOVE, "oppositeDirection" : true, "depth" : 1.5 * mm, "offsetDistance" : 25 * mm});
        }
    });
